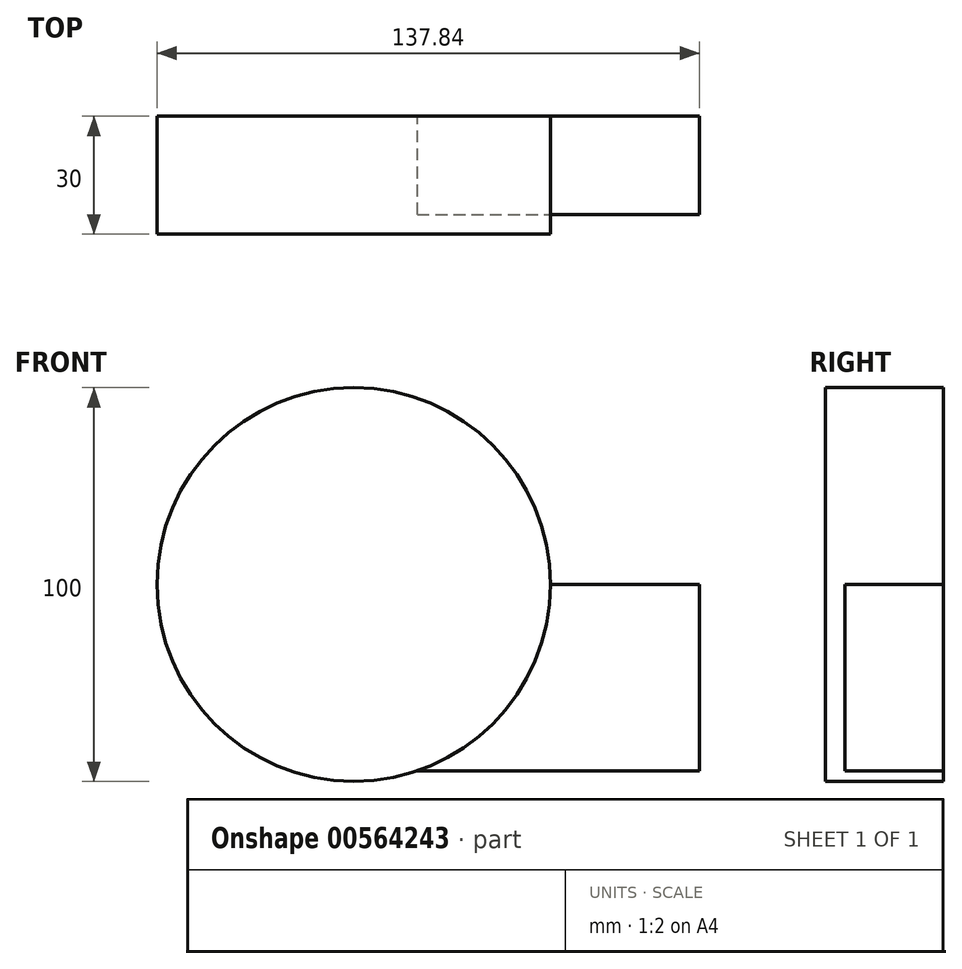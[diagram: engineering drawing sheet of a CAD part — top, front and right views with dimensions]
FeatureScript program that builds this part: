
annotation { "Feature Type Name" : "Feature", "Feature Type Description" : "" }
export const myFeature = defineFeature(function(context is Context, id is Id, definition is map)
    precondition{}
    {
        {
            var Q0;
            Q0=qCreatedBy(makeId("Front.planeOp"),FACE);
            var sketch = newSketch(context, id + "F0", { "sketchPlane" : qUnion([Q0])});
            skCircle(sketch, "E0", {"center": v(0, 0) * mm, "radius": 50 * mm});
            skSolve(sketch);
        }
        {
            var Q0;
            Q0 = qSketchRegion(id + "F0", true);
            extrude(context, id + "F1", {"entities" : qUnion([Q0]), "depth" : 30 * mm, "offsetDistance" : 25 * mm});
        }
        {
            var Q0;
            Q0=qCreatedBy(makeId("Front.planeOp"),FACE);
            var sketch = newSketch(context, id + "F2", { "sketchPlane" : qUnion([Q0])});
            skLineSegment(sketch, "E1.bottom", {"start": v(0, 0) * mm, "end": v(87.84, 0) * mm});
            skLineSegment(sketch, "E1.top", {"start": v(0, -47.3) * mm, "end": v(87.84, -47.3) * mm});
            skLineSegment(sketch, "E1.left", {"start": v(0, 0) * mm, "end": v(0, -47.3) * mm});
            skLineSegment(sketch, "E1.right", {"start": v(87.84, 0) * mm, "end": v(87.84, -47.3) * mm});
            skSolve(sketch);
        }
        {
            var Q0;
            Q0 = qSketchRegion(id + "F2", true);
            extrude(context, id + "F3", {"entities" : qUnion([Q0]), "operationType" : NewBodyOperationType.ADD, "depth" : 25 * mm, "offsetDistance" : 25 * mm});
        }
    });
